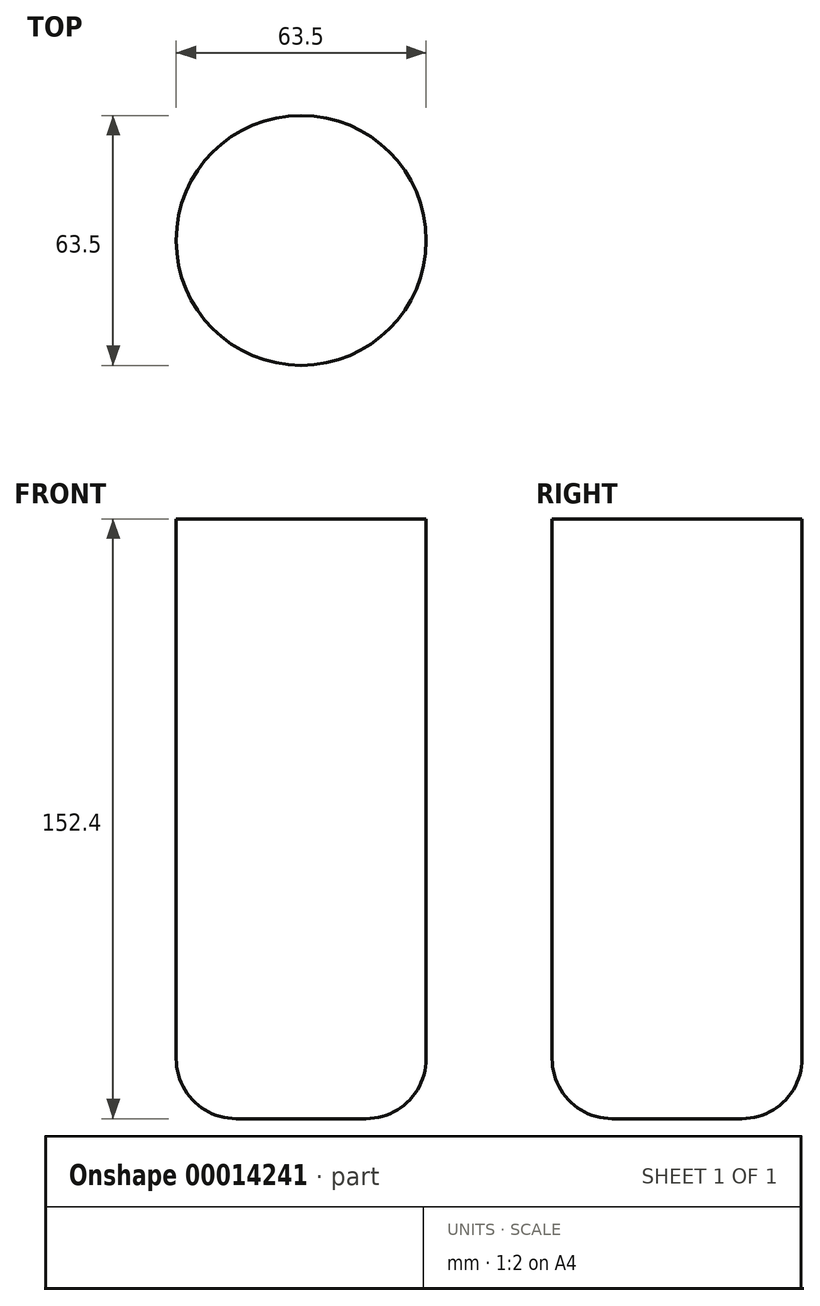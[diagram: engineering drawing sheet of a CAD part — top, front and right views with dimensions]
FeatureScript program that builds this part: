
annotation { "Feature Type Name" : "Feature", "Feature Type Description" : "" }
export const myFeature = defineFeature(function(context is Context, id is Id, definition is map)
    precondition{}
    {
        {
            var Q0;
            Q0=qCreatedBy(makeId("Top.planeOp"),FACE);
            var sketch = newSketch(context, id + "F0", { "sketchPlane" : qUnion([Q0])});
            skCircle(sketch, "E0", {"center": v(0, 0) * mm, "radius": 31.75 * mm});
            skSolve(sketch);
        }
        {
            var Q0;
            Q0=makeQuery(id+"F0.imprint","IMPRINT",FACE,{"disambiguationData":[TD([[makeQuery(id+"F0.imprint","IMPRINT",EDGE,{"derivedFrom":sQuery(id+"F0.wireOp",EDGE,"E0")}),1.0]])]});
            extrude(context, id + "F1", {"entities" : qUnion([Q0]), "endBound" : BoundingType.SYMMETRIC, "depth" : 152.4 * mm});
        }
        {
            var Q0;
            Q0=makeQuery(id+"F1.opExtrude","CAP_EDGE",EDGE,{"disambiguationData":[OSD([sQuery(id+"F0.wireOp",EDGE,"E0")])],"isStart":true});
            fillet(context, id + "F2", {"entities" : qUnion([Q0]), "radius" : 15.24 * mm, "tangentPropagation" : true, "allowEdgeOverflow" : false});
        }
    });
